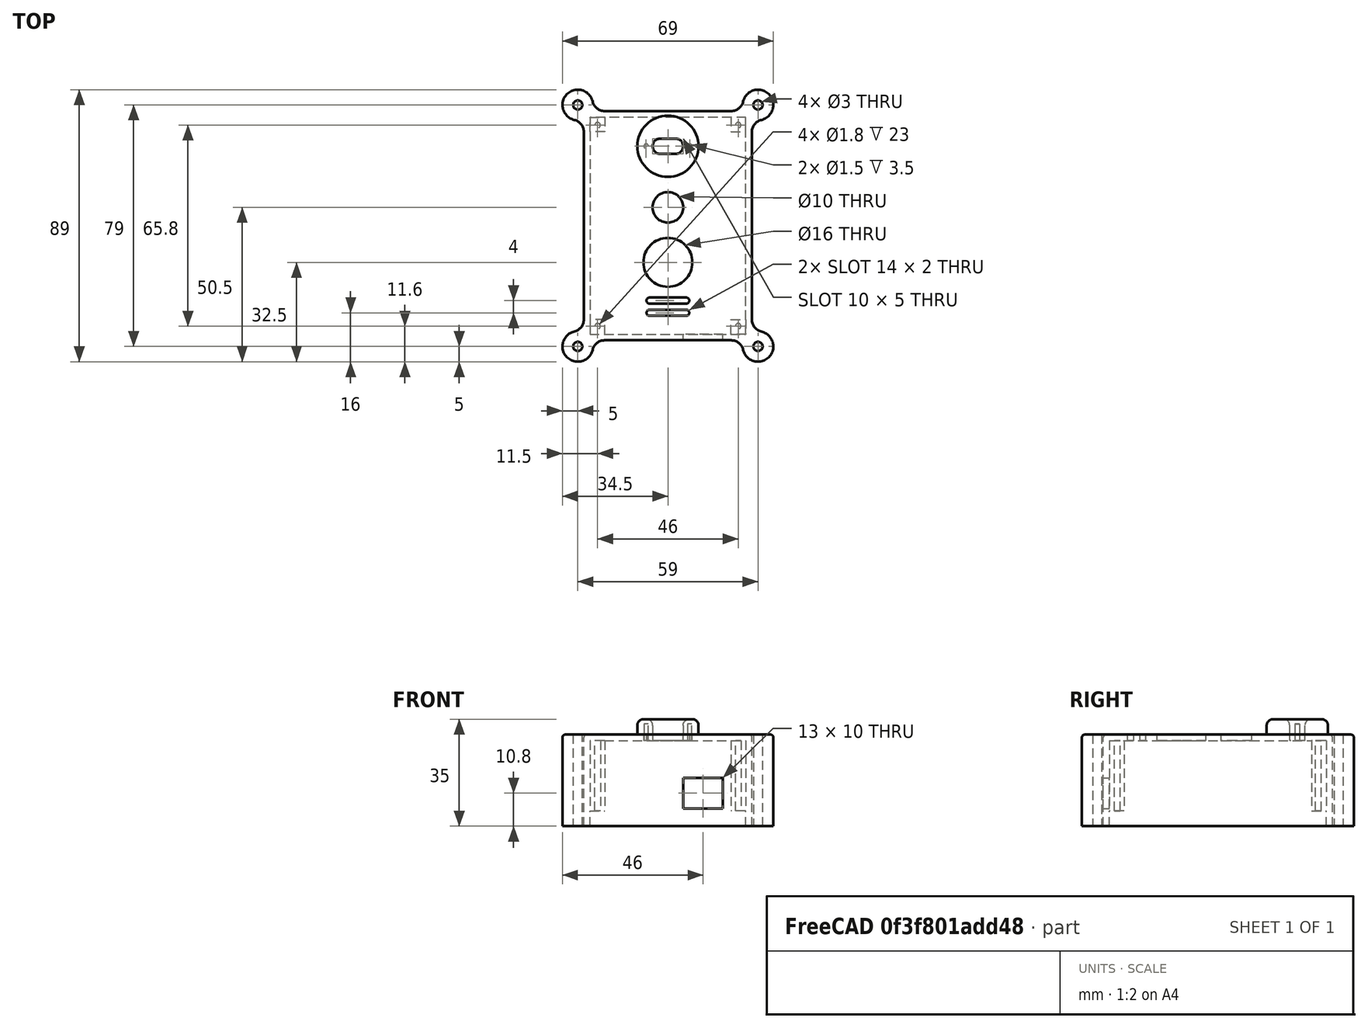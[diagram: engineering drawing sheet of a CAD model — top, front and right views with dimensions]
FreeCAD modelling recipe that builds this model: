
FCSTD DOCUMENT  (FreeCAD 0.18R16110 (Git))
Label: Boitier
License: All rights reserved
LicenseURL: http://en.wikipedia.org/wiki/All_rights_reserved
objects: Sketcher::SketchObject×13, PartDesign::Pocket×7, PartDesign::Pad×6, PartDesign::Fillet×4, PartDesign::Body×2, PartDesign::ShapeBinder×1, Mesh::Feature×1
note: 46 computed .brp shape members not serialized (recipe doc carries the construction recipe); baked Part::Feature solids carry a one-line shape summary decoded from their .brp

FEATURE [Sketcher::SketchObject] Sketch
  MapMode = 5
  Support = -> [XY_Plane]
  sketch-geometry (12):
    g0: ArcOfCircle CenterX=-29.5 CenterY=39.5 CenterZ=0 NormalX=0 NormalY=0 NormalZ=1 AngleXU=0 Radius=5 StartAngle=5.87167 EndAngle=11.4071
    g1: ArcOfCircle CenterX=29.5 CenterY=39.5 CenterZ=0 NormalX=0 NormalY=0 NormalZ=1 AngleXU=0 Radius=5 StartAngle=4.30087 EndAngle=9.83629
    g2: ArcOfCircle CenterX=-29.5 CenterY=-39.5 CenterZ=0 NormalX=0 NormalY=0 NormalZ=1 AngleXU=0 Radius=5 StartAngle=1.15928 EndAngle=6.6947
    g3: ArcOfCircle CenterX=29.5 CenterY=-39.5 CenterZ=0 NormalX=0 NormalY=0 NormalZ=1 AngleXU=0 Radius=5 StartAngle=2.73008 EndAngle=8.2655
    g4: LineSegment StartX=27.5 StartY=34.9174 StartZ=0 EndX=27.5 EndY=-34.9174 EndZ=0
    g5: LineSegment StartX=-27.5 StartY=34.9174 StartZ=0 EndX=-27.5 EndY=-34.9174 EndZ=0
    g6: LineSegment StartX=-24.9174 StartY=-37.5 StartZ=0 EndX=24.9174 EndY=-37.5 EndZ=0
    g7: LineSegment StartX=-24.9174 StartY=37.5 StartZ=0 EndX=24.9174 EndY=37.5 EndZ=0
    g8: Circle CenterX=-29.5 CenterY=39.5 CenterZ=0 NormalX=0 NormalY=0 NormalZ=1 AngleXU=0 Radius=1.5
    g9: Circle CenterX=29.5 CenterY=39.5 CenterZ=0 NormalX=0 NormalY=0 NormalZ=1 AngleXU=0 Radius=1.5
    g10: Circle CenterX=-29.5 CenterY=-39.5 CenterZ=0 NormalX=0 NormalY=0 NormalZ=1 AngleXU=0 Radius=1.5
    g11: Circle CenterX=29.5 CenterY=-39.5 CenterZ=0 NormalX=0 NormalY=0 NormalZ=1 AngleXU=0 Radius=1.5
  constraints (31):
    c: Coincident(g4,g1)
    c: Coincident(g4,g3)
    c: Vertical(g4)
    c: Coincident(g5,g0)
    c: Coincident(g5,g2)
    c: Vertical(g5)
    c: Coincident(g6,g2)
    c: Coincident(g6,g3)
    c: Horizontal(g6)
    c: Coincident(g7,g0)
    c: Horizontal(g7)
    c: Symmetric(g0,g2,g-1)
    c: Symmetric(g1,g3,g-1)
    c: Symmetric(g1,g0,g-2)
    c: Radius(g0) = 5
    c: Equal(g0,g3)
    c: Symmetric(g0,g1,g-2)
    c: Symmetric(g0,g2,g-1)
    c: DistanceX(g-2,g0) = -27.5
    c: DistanceY(g-1,g0) = 37.5
    c: Coincident(g1,g7)
    c: Distance(g0,g5) = 2
    c: Distance(g0,g7) = 2
    c: Coincident(g8,g0)
    c: Coincident(g9,g1)
    c: Coincident(g10,g2)
    c: Coincident(g11,g3)
    c: Radius(g11) = 1.5
    c: Equal(g11,g10)
    c: Equal(g11,g8)
    c: Equal(g11,g9)
FEATURE [PartDesign::Pad] Pad  label="Envelope externe"
  Length = 30
  Length2 = 100
  Profile = -> Sketch
  Type = 0
FEATURE [Sketcher::SketchObject] Sketch001
  MapMode = 5
  Placement = pos=(0,0,0) rot=(1,0,0;3.14159rad)
  Support = -> [Pad]
  sketch-geometry (4):
    g0: LineSegment StartX=-25.5 StartY=35.5 StartZ=0 EndX=25.5 EndY=35.5 EndZ=0
    g1: LineSegment StartX=25.5 StartY=35.5 StartZ=0 EndX=25.5 EndY=-35.5 EndZ=0
    g2: LineSegment StartX=25.5 StartY=-35.5 StartZ=0 EndX=-25.5 EndY=-35.5 EndZ=0
    g3: LineSegment StartX=-25.5 StartY=-35.5 StartZ=0 EndX=-25.5 EndY=35.5 EndZ=0
  constraints (10):
    c: Coincident(g0,g1)
    c: Coincident(g1,g2)
    c: Coincident(g2,g3)
    c: Coincident(g3,g0)
    c: Horizontal(g2)
    c: Vertical(g1)
    c: Symmetric(g0,g2,g-1)
    c: Symmetric(g0,g0,g-2)
    c: DistanceX(g0,g0) = 51
    c: DistanceY(g1,g1) = 71
FEATURE [PartDesign::Pocket] Pocket  label="Cavite interne"
  BaseFeature = -> Pad
  Length = 28
  Length2 = 100
  Profile = -> Sketch001
  Type = 0
FEATURE [Sketcher::SketchObject] Sketch002
  ExternalGeometry = -> [Pocket]
  MapMode = 5
  Placement = pos=(0,0,28) rot=(1,0,0;3.14159rad)
  Support = -> [Pocket]
  sketch-geometry (5):
    g0: Circle CenterX=-23 CenterY=32.9 CenterZ=0 NormalX=0 NormalY=0 NormalZ=1 AngleXU=0 Radius=0.9
    g1: LineSegment StartX=-25.5 StartY=35.5 StartZ=0 EndX=-20.7 EndY=35.5 EndZ=0
    g2: LineSegment StartX=-20.7 StartY=35.5 StartZ=0 EndX=-20.7 EndY=30.7 EndZ=0
    g3: LineSegment StartX=-20.7 StartY=30.7 StartZ=0 EndX=-25.5 EndY=30.7 EndZ=0
    g4: LineSegment StartX=-25.5 StartY=30.7 StartZ=0 EndX=-25.5 EndY=35.5 EndZ=0
  constraints (14):
    c: Coincident(g1,g2)
    c: Coincident(g2,g3)
    c: Coincident(g3,g4)
    c: Coincident(g4,g1)
    c: Horizontal(g1)
    c: Horizontal(g3)
    c: Vertical(g2)
    c: Vertical(g4)
    c: Coincident(g1,g-4)
    c: Radius(g0) = 0.9
    c: Distance(g3) = 4.8
    c: DistanceX(g-2,g0) = -23
    c: DistanceY(g-1,g0) = 32.9
    c: Distance(g2) = 4.8
FEATURE [PartDesign::Pad] Pad001  label="Pilier PCB 1"
  BaseFeature = -> Pocket
  Length = 23
  Length2 = 100
  Profile = -> Sketch002
  Type = 0
FEATURE [Sketcher::SketchObject] Sketch003
  ExternalGeometry = -> [Pad001]
  MapMode = 5
  Placement = pos=(0,0,28) rot=(1,0,0;3.14159rad)
  Support = -> [Pad001]
  sketch-geometry (5):
    g0: LineSegment StartX=25.5 StartY=35.5 StartZ=0 EndX=20.7 EndY=35.5 EndZ=0
    g1: LineSegment StartX=20.7 StartY=35.5 StartZ=0 EndX=20.7 EndY=30.7 EndZ=0
    g2: LineSegment StartX=20.7 StartY=30.7 StartZ=0 EndX=25.5 EndY=30.7 EndZ=0
    g3: LineSegment StartX=25.5 StartY=30.7 StartZ=0 EndX=25.5 EndY=35.5 EndZ=0
    g4: Circle CenterX=23 CenterY=32.9 CenterZ=0 NormalX=0 NormalY=0 NormalZ=1 AngleXU=0 Radius=0.9
  constraints (14):
    c: Coincident(g0,g1)
    c: Coincident(g1,g2)
    c: Coincident(g2,g3)
    c: Coincident(g3,g0)
    c: Horizontal(g0)
    c: Horizontal(g2)
    c: Vertical(g1)
    c: Vertical(g3)
    c: Coincident(g0,g-4)
    c: DistanceY(g1,g1) = 4.8
    c: DistanceX(g2,g2) = 4.8
    c: Radius(g4) = 0.9
    c: DistanceX(g-2,g4) = 23
    c: DistanceY(g-1,g4) = 32.9
FEATURE [PartDesign::Pad] Pad002  label="Pilier PCB 2"
  BaseFeature = -> Pad001
  Length = 23
  Length2 = 100
  Profile = -> Sketch003
  Type = 0
FEATURE [Sketcher::SketchObject] Sketch004
  ExternalGeometry = -> [Pad002]
  MapMode = 5
  Placement = pos=(0,0,28) rot=(1,0,0;3.14159rad)
  Support = -> [Pad002]
  sketch-geometry (5):
    g0: LineSegment StartX=25.5 StartY=-35.5 StartZ=0 EndX=20.7 EndY=-35.5 EndZ=0
    g1: LineSegment StartX=20.7 StartY=-35.5 StartZ=0 EndX=20.7 EndY=-30.7 EndZ=0
    g2: LineSegment StartX=20.7 StartY=-30.7 StartZ=0 EndX=25.5 EndY=-30.7 EndZ=0
    g3: LineSegment StartX=25.5 StartY=-30.7 StartZ=0 EndX=25.5 EndY=-35.5 EndZ=0
    g4: Circle CenterX=23 CenterY=-32.9 CenterZ=0 NormalX=0 NormalY=0 NormalZ=1 AngleXU=0 Radius=0.9
  constraints (14):
    c: Coincident(g0,g1)
    c: Coincident(g1,g2)
    c: Coincident(g2,g3)
    c: Coincident(g3,g0)
    c: Horizontal(g0)
    c: Horizontal(g2)
    c: Vertical(g1)
    c: Vertical(g3)
    c: Coincident(g0,g-4)
    c: DistanceX(g2,g2) = 4.8
    c: DistanceY(g1,g1) = 4.8
    c: Radius(g4) = 0.9
    c: DistanceX(g-2,g4) = 23
    c: DistanceY(g-1,g4) = -32.9
FEATURE [PartDesign::Pad] Pad003  label="Pilier PCB 3"
  BaseFeature = -> Pad002
  Length = 23
  Length2 = 100
  Profile = -> Sketch004
  Type = 0
FEATURE [Sketcher::SketchObject] Sketch005
  ExternalGeometry = -> [Pad003]
  MapMode = 5
  Placement = pos=(0,0,28) rot=(1,0,0;3.14159rad)
  Support = -> [Pad003]
  sketch-geometry (5):
    g0: LineSegment StartX=-25.5 StartY=-35.5 StartZ=0 EndX=-20.7 EndY=-35.5 EndZ=0
    g1: LineSegment StartX=-20.7 StartY=-35.5 StartZ=0 EndX=-20.7 EndY=-30.7 EndZ=0
    g2: LineSegment StartX=-20.7 StartY=-30.7 StartZ=0 EndX=-25.5 EndY=-30.7 EndZ=0
    g3: LineSegment StartX=-25.5 StartY=-30.7 StartZ=0 EndX=-25.5 EndY=-35.5 EndZ=0
    g4: Circle CenterX=-23 CenterY=-32.9 CenterZ=0 NormalX=0 NormalY=0 NormalZ=1 AngleXU=0 Radius=0.9
  constraints (14):
    c: Coincident(g0,g1)
    c: Coincident(g1,g2)
    c: Coincident(g2,g3)
    c: Coincident(g3,g0)
    c: Horizontal(g0)
    c: Horizontal(g2)
    c: Vertical(g1)
    c: Vertical(g3)
    c: Coincident(g0,g-4)
    c: DistanceX(g2,g2) = 4.8
    c: DistanceY(g1,g1) = 4.8
    c: Radius(g4) = 0.9
    c: DistanceX(g-2,g4) = -23
    c: DistanceY(g-1,g4) = -32.9
FEATURE [PartDesign::Pad] Pad004  label="Pilier PCB 4"
  BaseFeature = -> Pad003
  Length = 23
  Length2 = 100
  Profile = -> Sketch005
  Type = 0
FEATURE [Sketcher::SketchObject] Sketch006
  ExternalGeometry = -> [Pad004]
  MapMode = 5
  Placement = pos=(0,0,28) rot=(1,0,0;3.14159rad)
  Support = -> [Pad004]
  sketch-geometry (1):
    g0: Circle CenterX=0 CenterY=-6 CenterZ=0 NormalX=0 NormalY=0 NormalZ=1 AngleXU=0 Radius=5
  constraints (3):
    c: PointOnObject(g0,g-2)
    c: Distance(g0,g-3) = 41.5
    c: Radius(g0) = 5
FEATURE [PartDesign::Pocket] Pocket001  label="Percage LED"
  BaseFeature = -> Pad004
  Length = 5
  Length2 = 100
  Profile = -> Sketch006
  Type = 0
FEATURE [Sketcher::SketchObject] Sketch007
  MapMode = 5
  Placement = pos=(0,0,28) rot=(1,0,0;3.14159rad)
  Support = -> [Pocket001]
  sketch-geometry (1):
    g0: Circle CenterX=0 CenterY=12 CenterZ=0 NormalX=0 NormalY=0 NormalZ=1 AngleXU=0 Radius=8
  constraints (3):
    c: PointOnObject(g0,g-2)
    c: Radius(g0) = 8
    c: DistanceY(g-1,g0) = 12
FEATURE [PartDesign::Pocket] Pocket002  label="Percage bouton"
  BaseFeature = -> Pocket001
  Length = 5
  Length2 = 100
  Profile = -> Sketch007
  Type = 0
FEATURE [Sketcher::SketchObject] Sketch008
  ExternalGeometry = -> [Pocket002]
  MapMode = 5
  Placement = pos=(0,0,28) rot=(1,0,0;3.14159rad)
  Support = -> [Pocket002]
  sketch-geometry (8):
    g0: ArcOfCircle CenterX=-6 CenterY=28.5 CenterZ=0 NormalX=0 NormalY=0 NormalZ=1 AngleXU=0 Radius=1 StartAngle=1.5708 EndAngle=4.71239
    g1: ArcOfCircle CenterX=6 CenterY=28.5 CenterZ=0 NormalX=0 NormalY=0 NormalZ=1 AngleXU=0 Radius=1 StartAngle=4.71239 EndAngle=7.85398
    g2: LineSegment StartX=-6 StartY=27.5 StartZ=0 EndX=6 EndY=27.5 EndZ=0
    g3: LineSegment StartX=-6 StartY=29.5 StartZ=0 EndX=6 EndY=29.5 EndZ=0
    g4: ArcOfCircle CenterX=-6 CenterY=24.5 CenterZ=0 NormalX=0 NormalY=0 NormalZ=1 AngleXU=0 Radius=1 StartAngle=1.5708 EndAngle=4.71239
    g5: ArcOfCircle CenterX=6 CenterY=24.5 CenterZ=0 NormalX=0 NormalY=0 NormalZ=1 AngleXU=0 Radius=1 StartAngle=4.71239 EndAngle=7.85398
    g6: LineSegment StartX=-6 StartY=23.5 StartZ=0 EndX=6 EndY=23.5 EndZ=0
    g7: LineSegment StartX=-6 StartY=25.5 StartZ=0 EndX=6 EndY=25.5 EndZ=0
  constraints (18):
    c: Tangent(g0,g3) = 1.5708
    c: Tangent(g0,g2) = -1.5708
    c: Tangent(g2,g1) = -1.5708
    c: Tangent(g3,g1) = 1.5708
    c: Horizontal(g2)
    c: Tangent(g4,g7) = 1.5708
    c: Tangent(g4,g6) = -1.5708
    c: Tangent(g6,g5) = -1.5708
    c: Tangent(g7,g5) = 1.5708
    c: Horizontal(g6)
    c: Symmetric(g0,g1,g-2)
    c: Symmetric(g4,g5,g-2)
    c: Radius(g1) = 1
    c: Radius(g5) = 1
    c: Distance(g1,g7) = 2
    c: Distance(g3) = 12
    c: Distance(g7) = 12
    c: Distance(g1,g-3) = 6
FEATURE [PartDesign::Pocket] Pocket003  label="Percage buzzer"
  BaseFeature = -> Pocket002
  Length = 5
  Length2 = 100
  Profile = -> Sketch008
  Type = 0
FEATURE [Sketcher::SketchObject] Sketch009
  ExternalGeometry = -> [Pocket003]
  MapMode = 5
  Placement = pos=(0,-37.5,0) rot=(1,0,0;1.5708rad)
  Support = -> [Pocket003]
  sketch-geometry (4):
    g0: LineSegment StartX=5 StartY=15.8 StartZ=0 EndX=18 EndY=15.8 EndZ=0
    g1: LineSegment StartX=18 StartY=15.8 StartZ=0 EndX=18 EndY=5.8 EndZ=0
    g2: LineSegment StartX=18 StartY=5.8 StartZ=0 EndX=5 EndY=5.8 EndZ=0
    g3: LineSegment StartX=5 StartY=5.8 StartZ=0 EndX=5 EndY=15.8 EndZ=0
  constraints (12):
    c: Coincident(g0,g1)
    c: Coincident(g1,g2)
    c: Coincident(g2,g3)
    c: Coincident(g3,g0)
    c: Horizontal(g0)
    c: Horizontal(g2)
    c: Vertical(g1)
    c: Vertical(g3)
    c: DistanceX(g0,g0) = 13
    c: DistanceY(g1,g1) = 10
    c: DistanceX(g-2,g2) = 5
    c: Distance(g1,g-3) = 0.8
FEATURE [PartDesign::Pocket] Pocket004  label="Percage USB"
  BaseFeature = -> Pocket003
  Length = 5
  Length2 = 100
  Profile = -> Sketch009
  Type = 0
FEATURE [Sketcher::SketchObject] Sketch010
  ExternalGeometry = -> [Pocket004]
  MapMode = 5
  Placement = pos=(0,0,28) rot=(1,0,0;3.14159rad)
  Support = -> [Pocket004]
  sketch-geometry (6):
    g0: ArcOfCircle CenterX=-2.5 CenterY=-26 CenterZ=0 NormalX=0 NormalY=0 NormalZ=1 AngleXU=0 Radius=2.5 StartAngle=1.5708 EndAngle=4.71239
    g1: ArcOfCircle CenterX=2.5 CenterY=-26 CenterZ=0 NormalX=0 NormalY=0 NormalZ=1 AngleXU=0 Radius=2.5 StartAngle=4.71239 EndAngle=7.85398
    g2: LineSegment StartX=-2.5 StartY=-28.5 StartZ=0 EndX=2.5 EndY=-28.5 EndZ=0
    g3: LineSegment StartX=-2.5 StartY=-23.5 StartZ=0 EndX=2.5 EndY=-23.5 EndZ=0
    g4: Circle CenterX=-7.115 CenterY=-26 CenterZ=0 NormalX=0 NormalY=0 NormalZ=1 AngleXU=0 Radius=0.75
    g5: Circle CenterX=7.115 CenterY=-26 CenterZ=0 NormalX=0 NormalY=0 NormalZ=1 AngleXU=0 Radius=0.75
  constraints (14):
    c: Tangent(g0,g3) = 1.5708
    c: Tangent(g0,g2) = -1.5708
    c: Tangent(g2,g1) = -1.5708
    c: Tangent(g3,g1) = 1.5708
    c: Horizontal(g2)
    c: Radius(g1) = 2.5
    c: DistanceX(g3,g3) = 5
    c: Symmetric(g0,g1,g-2)
    c: Symmetric(g5,g4,g-2)
    c: DistanceX(g-2,g4) = -7.115
    c: Radius(g4) = 0.75
    c: Equal(g4,g5)
    c: DistanceY(g-1,g5) = -26
    c: DistanceY(g-1,g1) = -26
FEATURE [PartDesign::Pocket] Pocket005  label="Percage TOF10120"
  BaseFeature = -> Pocket004
  Length = 5
  Length2 = 100
  Profile = -> Sketch010
  Type = 0
FEATURE [PartDesign::ShapeBinder] CopyPocket005
  TraceSupport = false
FEATURE [Sketcher::SketchObject] Sketch011
  MapMode = 5
  Placement = pos=(0,0,30) rot=(0,0,1;0rad)
  Support = -> [CopyPocket005]
  sketch-geometry (5):
    g0: ArcOfCircle CenterX=-2.5 CenterY=26 CenterZ=0 NormalX=0 NormalY=0 NormalZ=1 AngleXU=0 Radius=2.5 StartAngle=1.5708 EndAngle=4.71239
    g1: ArcOfCircle CenterX=2.5 CenterY=26 CenterZ=0 NormalX=0 NormalY=0 NormalZ=1 AngleXU=0 Radius=2.5 StartAngle=4.71239 EndAngle=7.85398
    g2: LineSegment StartX=-2.5 StartY=23.5 StartZ=0 EndX=2.5 EndY=23.5 EndZ=0
    g3: LineSegment StartX=-2.5 StartY=28.5 StartZ=0 EndX=2.5 EndY=28.5 EndZ=0
    g4: Circle CenterX=0.000374 CenterY=26 CenterZ=0 NormalX=0 NormalY=0 NormalZ=1 AngleXU=0 Radius=10
  constraints (11):
    c: Tangent(g0,g3) = 1.5708
    c: Tangent(g0,g2) = -1.5708
    c: Tangent(g2,g1) = -1.5708
    c: Tangent(g3,g1) = 1.5708
    c: Horizontal(g2)
    c: Radius(g1) = 2.5
    c: DistanceX(g3,g3) = 5
    c: Symmetric(g1,g0,g-2)
    c: DistanceY(g-1,g1) = 26
    c: DistanceY(g-1,g4) = 26
    c: Radius(g4) = 10
FEATURE [PartDesign::Pad] Pad005  label="Forme generale"
  Length = 5
  Length2 = 100
  Profile = -> Sketch011
  Type = 0
FEATURE [PartDesign::Fillet] Fillet
  Base = -> Pad005 [Edge15]
  BaseFeature = -> Pad005
  Radius = 2
FEATURE [PartDesign::Fillet] Fillet001
  Base = -> Fillet [Edge22]
  BaseFeature = -> Fillet
  Radius = 2
FEATURE [Sketcher::SketchObject] Sketch012
  MapMode = 5
  Placement = pos=(0,0,30) rot=(1,0,0;3.14159rad)
  Support = -> [Fillet001]
  sketch-geometry (2):
    g0: Circle CenterX=-7.115 CenterY=-26 CenterZ=0 NormalX=0 NormalY=0 NormalZ=1 AngleXU=0 Radius=0.75
    g1: Circle CenterX=7.115 CenterY=-26 CenterZ=0 NormalX=0 NormalY=0 NormalZ=1 AngleXU=0 Radius=0.75
  constraints (5):
    c: Symmetric(g0,g1,g-2)
    c: Radius(g0) = 0.75
    c: Equal(g0,g1)
    c: DistanceY(g-1,g0) = -26
    c: DistanceX(g-2,g0) = -7.115
FEATURE [PartDesign::Pocket] Pocket006
  BaseFeature = -> Fillet001
  Length = 3.5
  Length2 = 100
  Profile = -> Sketch012
  Type = 0
FEATURE [PartDesign::Body] Body001  label="Protecteur TOF"
  Group = -> [CopyPocket005,Sketch011,Pad005,Fillet,Fillet001,Sketch012,Pocket006]
  Origin = -> Origin001
  Tip = -> Pocket006
FEATURE [Mesh::Feature] Mesh  label="Protecteur TOF (Meshed)"
FEATURE [PartDesign::Fillet] Fillet002
  Base = -> Pocket005 [Edge2,Edge1,Edge49,Edge5,Edge50,Edge8,Edge51,Edge52]
  BaseFeature = -> Pocket005
  Radius = 4
FEATURE [PartDesign::Fillet] Fillet003
  Base = -> Fillet002 [Edge40]
  BaseFeature = -> Fillet002
  Radius = 1
FEATURE [PartDesign::Body] Body  label="Boitier PCB"
  Group = -> [Sketch,Pad,Sketch001,Pocket,Sketch002,Pad001,Sketch003,Pad002,Sketch004,Pad003,Sketch005,Pad004,Sketch006,Pocket001,Sketch007,Pocket002,Sketch008,Pocket003,Sketch009,Pocket004,Sketch010,Pocket005,Fillet002,Fillet003]
  Origin = -> Origin
  Tip = -> Fillet003
